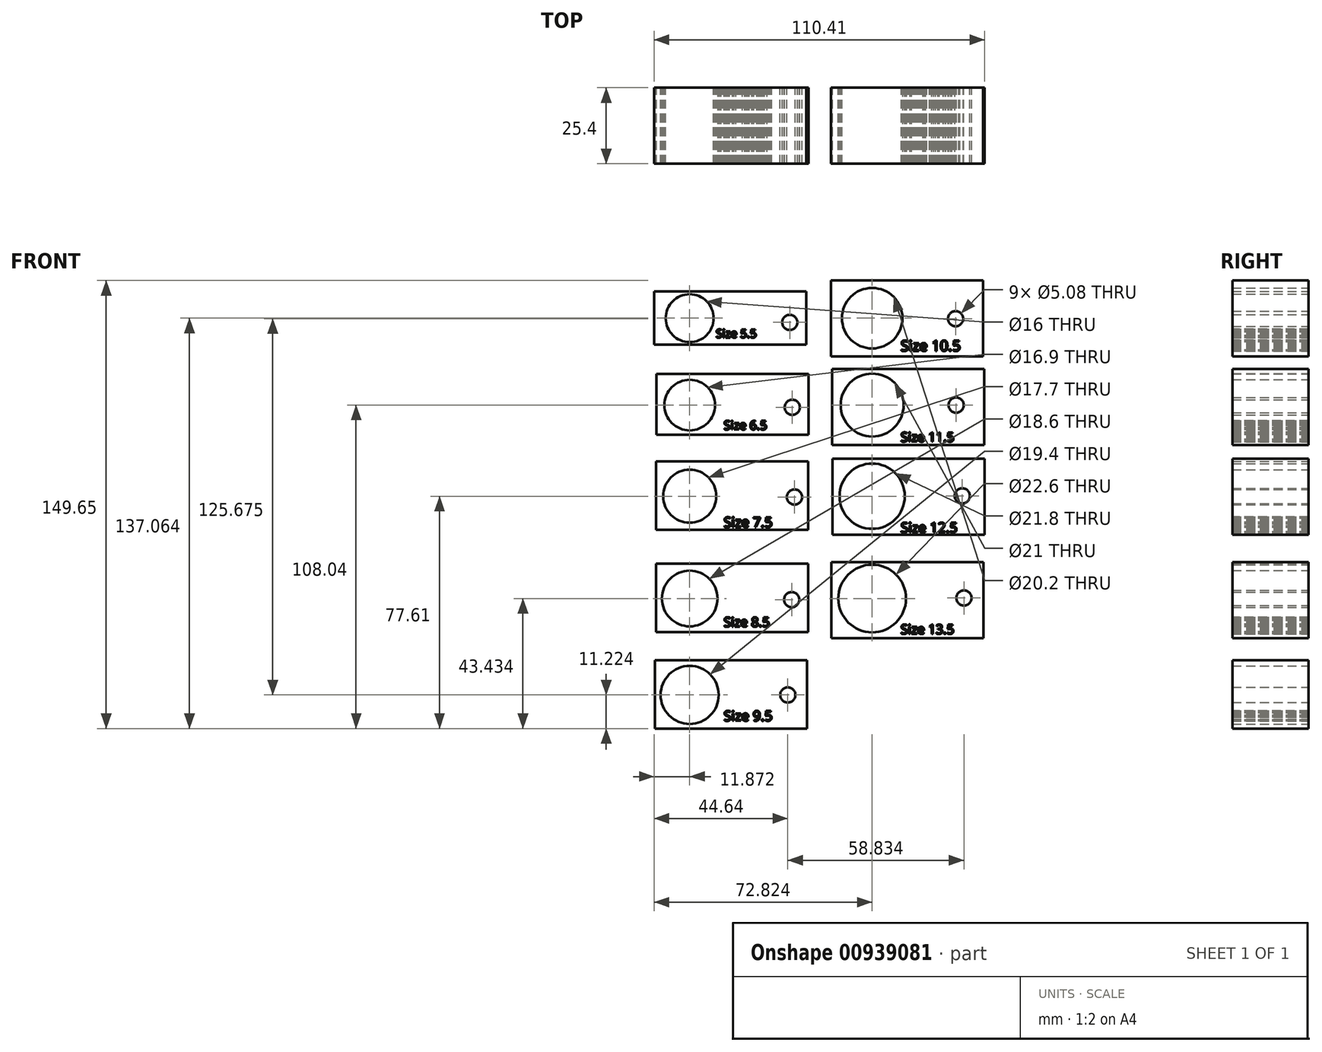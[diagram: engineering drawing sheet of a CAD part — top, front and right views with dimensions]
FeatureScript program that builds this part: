
annotation { "Feature Type Name" : "Feature", "Feature Type Description" : "" }
export const myFeature = defineFeature(function(context is Context, id is Id, definition is map)
    precondition{}
    {
        {
            var Q0;
            Q0=qCreatedBy(makeId("Front.planeOp"),FACE);
            var sketch = newSketch(context, id + "F0", { "sketchPlane" : qUnion([Q0])});
            skCircle(sketch, "E0", {"center": v(-57.17, 59.45) * mm, "radius": 8 * mm});
            skCircle(sketch, "E1", {"center": v(-57.17, 30.43) * mm, "radius": 8.45 * mm});
            skCircle(sketch, "E2", {"center": v(-57.17, 0) * mm, "radius": 8.85 * mm});
            skCircle(sketch, "E3", {"center": v(-57.17, -34.18) * mm, "radius": 9.3 * mm});
            skCircle(sketch, "E4", {"center": v(-57.17, -66.39) * mm, "radius": 9.7 * mm});
            skCircle(sketch, "E5", {"center": v(3.78, -34.18) * mm, "radius": 11.3 * mm});
            skCircle(sketch, "E6", {"center": v(3.78, 0) * mm, "radius": 10.9 * mm});
            skCircle(sketch, "E7", {"center": v(3.78, 30.43) * mm, "radius": 10.5 * mm});
            skCircle(sketch, "E8", {"center": v(3.78, 59.45) * mm, "radius": 10.1 * mm});
            skLineSegment(sketch, "E9.bottom", {"start": v(-69.04, 68.41) * mm, "end": v(-18.24, 68.41) * mm});
            skLineSegment(sketch, "E9.top", {"start": v(-69.04, 50.63) * mm, "end": v(-18.24, 50.63) * mm});
            skLineSegment(sketch, "E9.left", {"start": v(-69.04, 68.41) * mm, "end": v(-69.04, 50.63) * mm});
            skLineSegment(sketch, "E9.right", {"start": v(-18.24, 68.41) * mm, "end": v(-18.24, 50.63) * mm});
            skLineSegment(sketch, "E10.bottom", {"start": v(-68.28, 40.88) * mm, "end": v(-17.48, 40.88) * mm});
            skLineSegment(sketch, "E10.top", {"start": v(-68.28, 20.56) * mm, "end": v(-17.48, 20.56) * mm});
            skLineSegment(sketch, "E10.left", {"start": v(-68.28, 40.88) * mm, "end": v(-68.28, 20.56) * mm});
            skLineSegment(sketch, "E10.right", {"start": v(-17.48, 40.88) * mm, "end": v(-17.48, 20.56) * mm});
            skLineSegment(sketch, "E11.bottom", {"start": v(-68.4, 11.61) * mm, "end": v(-17.6, 11.61) * mm});
            skLineSegment(sketch, "E11.top", {"start": v(-68.4, -11.25) * mm, "end": v(-17.6, -11.25) * mm});
            skLineSegment(sketch, "E11.left", {"start": v(-68.4, 11.61) * mm, "end": v(-68.4, -11.25) * mm});
            skLineSegment(sketch, "E11.right", {"start": v(-17.6, 11.61) * mm, "end": v(-17.6, -11.25) * mm});
            skLineSegment(sketch, "E12.bottom", {"start": v(-68.43, -22.5) * mm, "end": v(-17.63, -22.5) * mm});
            skLineSegment(sketch, "E12.top", {"start": v(-68.43, -45.35) * mm, "end": v(-17.63, -45.35) * mm});
            skLineSegment(sketch, "E12.left", {"start": v(-68.43, -22.5) * mm, "end": v(-68.43, -45.35) * mm});
            skLineSegment(sketch, "E12.right", {"start": v(-17.63, -22.5) * mm, "end": v(-17.63, -45.35) * mm});
            skLineSegment(sketch, "E13.bottom", {"start": v(-68.79, -54.75) * mm, "end": v(-17.99, -54.75) * mm});
            skLineSegment(sketch, "E13.top", {"start": v(-68.79, -77.61) * mm, "end": v(-17.99, -77.61) * mm});
            skLineSegment(sketch, "E13.left", {"start": v(-68.79, -54.75) * mm, "end": v(-68.79, -77.61) * mm});
            skLineSegment(sketch, "E13.right", {"start": v(-17.99, -54.75) * mm, "end": v(-17.99, -77.61) * mm});
            skLineSegment(sketch, "E14.bottom", {"start": v(-9.8, -21.98) * mm, "end": v(41, -21.98) * mm});
            skLineSegment(sketch, "E14.top", {"start": v(-9.8, -47.38) * mm, "end": v(41, -47.38) * mm});
            skLineSegment(sketch, "E14.left", {"start": v(-9.8, -21.98) * mm, "end": v(-9.8, -47.38) * mm});
            skLineSegment(sketch, "E14.right", {"start": v(41, -21.98) * mm, "end": v(41, -47.38) * mm});
            skLineSegment(sketch, "E15.bottom", {"start": v(-9.43, 12.5) * mm, "end": v(41.37, 12.5) * mm});
            skLineSegment(sketch, "E15.top", {"start": v(-9.43, -12.9) * mm, "end": v(41.37, -12.9) * mm});
            skLineSegment(sketch, "E15.left", {"start": v(-9.43, 12.5) * mm, "end": v(-9.43, -12.9) * mm});
            skLineSegment(sketch, "E15.right", {"start": v(41.37, 12.5) * mm, "end": v(41.37, -12.9) * mm});
            skLineSegment(sketch, "E16.bottom", {"start": v(-9.62, 42.55) * mm, "end": v(41.18, 42.55) * mm});
            skLineSegment(sketch, "E16.top", {"start": v(-9.62, 17.15) * mm, "end": v(41.18, 17.15) * mm});
            skLineSegment(sketch, "E16.left", {"start": v(-9.62, 42.55) * mm, "end": v(-9.62, 17.15) * mm});
            skLineSegment(sketch, "E16.right", {"start": v(41.18, 42.55) * mm, "end": v(41.18, 17.15) * mm});
            skLineSegment(sketch, "E17.bottom", {"start": v(-9.99, 72.04) * mm, "end": v(40.81, 72.04) * mm});
            skLineSegment(sketch, "E17.top", {"start": v(-9.99, 46.64) * mm, "end": v(40.81, 46.64) * mm});
            skLineSegment(sketch, "E17.left", {"start": v(-9.99, 72.04) * mm, "end": v(-9.99, 46.64) * mm});
            skLineSegment(sketch, "E17.right", {"start": v(40.81, 72.04) * mm, "end": v(40.81, 46.64) * mm});
            skCircle(sketch, "E18", {"center": v(-23.74, 58.05) * mm, "radius": 2.54 * mm});
            skCircle(sketch, "E19", {"center": v(-22.91, 29.68) * mm, "radius": 2.54 * mm});
            skCircle(sketch, "E20", {"center": v(-22.17, -0.3) * mm, "radius": 2.54 * mm});
            skCircle(sketch, "E21", {"center": v(-23.1, -34.55) * mm, "radius": 2.54 * mm});
            skCircle(sketch, "E22", {"center": v(-24.4, -66.39) * mm, "radius": 2.54 * mm});
            skCircle(sketch, "E23", {"center": v(34.43, -34) * mm, "radius": 2.54 * mm});
            skCircle(sketch, "E24", {"center": v(33.88, 0.08) * mm, "radius": 2.54 * mm});
            skCircle(sketch, "E25", {"center": v(31.83, 30.43) * mm, "radius": 2.54 * mm});
            skCircle(sketch, "E26", {"center": v(31.64, 59.29) * mm, "radius": 2.54 * mm});
            skSolve(sketch);
        }
        {
            var Q0;
            Q0=qCreatedBy(makeId("Front.planeOp"),FACE);
            var sketch = newSketch(context, id + "F1", { "sketchPlane" : qUnion([Q0])});
            skText(sketch, "E27", { "text": "Size 5.5", "fontName": "OpenSans-Regular.ttf"});
            skText(sketch, "E28", { "text": "Size 6.5", "fontName": "OpenSans-Regular.ttf"});
            skText(sketch, "E29", { "text": "Size 7.5", "fontName": "OpenSans-Regular.ttf"});
            skText(sketch, "E30", { "text": "Size 8.5", "fontName": "OpenSans-Regular.ttf"});
            skPoint(sketch, "E30.firstSnap0", {"position": v(-45.81, -8.67) * mm});
            skText(sketch, "E31", { "text": "Size 9.5", "fontName": "OpenSans-Regular.ttf"});
            skText(sketch, "E32", { "text": "Size 10.5", "fontName": "OpenSans-Regular.ttf"});
            skText(sketch, "E33", { "text": "Size 11.5", "fontName": "OpenSans-Regular.ttf"});
            skText(sketch, "E34", { "text": "Size 12.5", "fontName": "OpenSans-Regular.ttf"});
            skText(sketch, "E35", { "text": "Size 13.5", "fontName": "OpenSans-Regular.ttf"});
            const initialGuessF1  = {"E27": [-0.04842, 0.05296, 1, 0, 0.0028], "E28": [-0.04581, 0.02224, 1, 0, 0.00298], "E29": [-0.04581, -0.01034, 1, 0, 0.00335], "E30": [-0.04581, -0.0436, 1, 0, 0.00316], "E31": [-0.04581, -0.07504, 1, 0, 0.00335], "E32": [0.0133, 0.0485, 1, 0, 0.00354], "E33": [0.0133, 0.01818, 1, 0, 0.00316], "E34": [0.0133, -0.01215, 1, 0, 0.00335], "E35": [0.0133, -0.04601, 1, 0, 0.00316]};
            skSetInitialGuess(sketch, initialGuessF1);
            skSolve(sketch);
        }
        {
            var Q0;
            Q0 = qSketchRegion(id + "F0", true);
            extrude(context, id + "F2", {"entities" : qUnion([Q0]), "depth" : 25.4 * mm, "offsetDistance" : 25.4 * mm});
        }
        {
            var Q0;
            Q0 = qSketchRegion(id + "F1", true);
            extrude(context, id + "F3", {"entities" : qUnion([Q0]), "depth" : 25.4 * mm, "offsetDistance" : 25.4 * mm});
        }
    });
